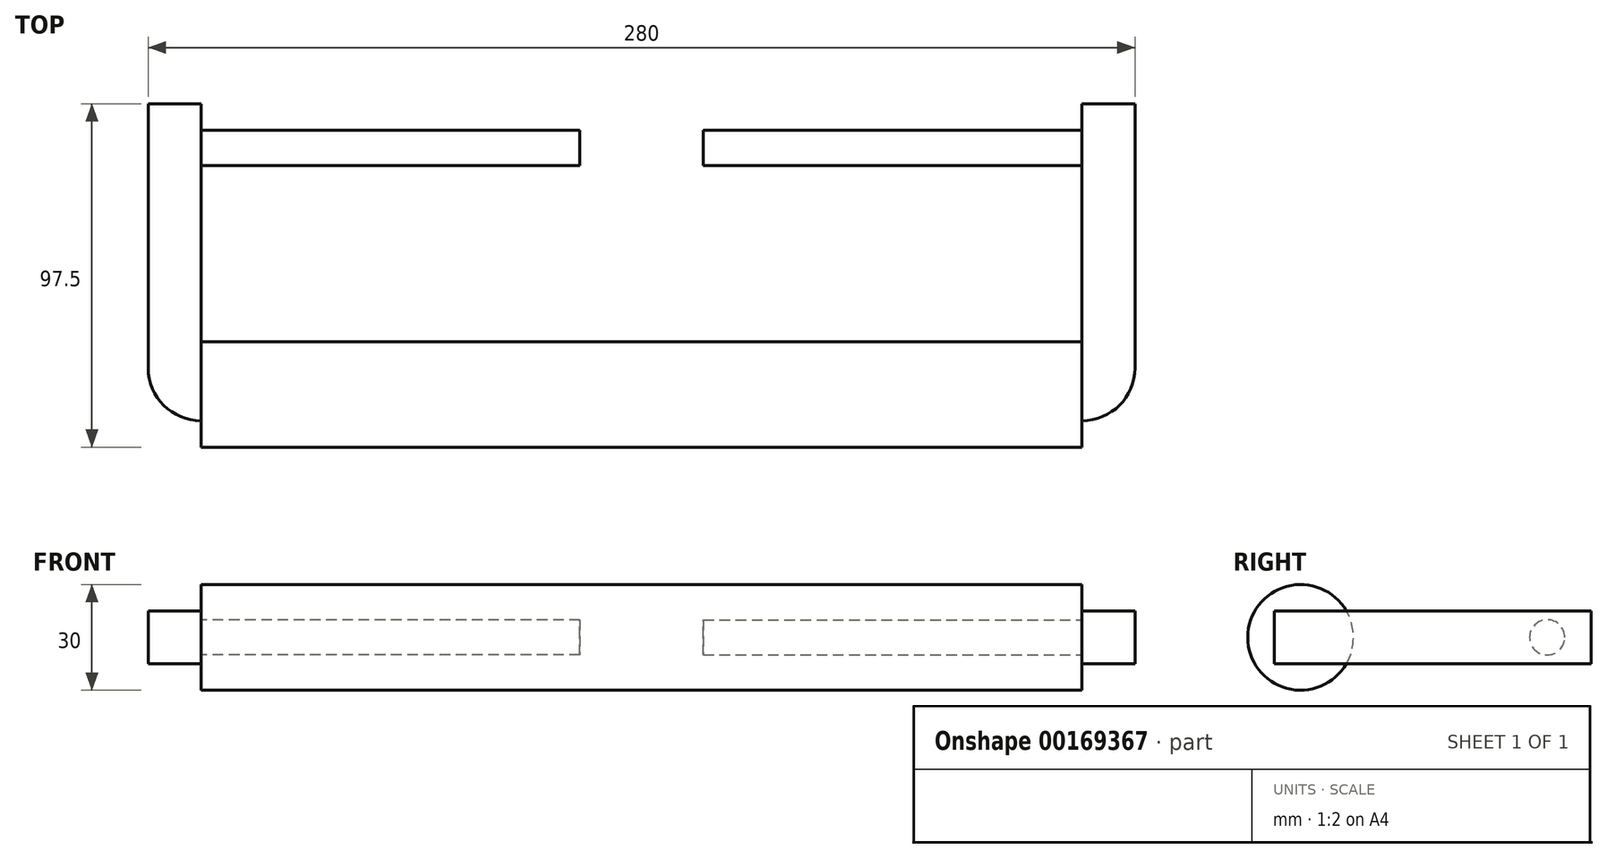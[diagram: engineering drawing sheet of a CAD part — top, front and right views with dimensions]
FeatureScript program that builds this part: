
annotation { "Feature Type Name" : "Feature", "Feature Type Description" : "" }
export const myFeature = defineFeature(function(context is Context, id is Id, definition is map)
    precondition{}
    {
        {
            var Q0;
            Q0=qCreatedBy(makeId("Right.planeOp"),FACE);
            var sketch = newSketch(context, id + "F0", { "sketchPlane" : qUnion([Q0])});
            skCircle(sketch, "E0", {"center": v(0, 0) * mm, "radius": 15 * mm});
            skSolve(sketch);
        }
        {
            var Q0;
            Q0=makeQuery(id+"F0.imprint","IMPRINT",FACE,{"disambiguationData":[TD([[makeQuery(id+"F0.imprint","IMPRINT",EDGE,{"derivedFrom":sQuery(id+"F0.wireOp",EDGE,"E0")}),1.0]])]});
            extrude(context, id + "F1", {"entities" : qUnion([Q0]), "endBound" : BoundingType.SYMMETRIC, "depth" : 250 * mm});
        }
        {
            var Q0;
            Q0=makeQuery(id+"F1.opExtrude","CAP_FACE",FACE,{"disambiguationData":[OSD([sQuery(id+"F0.wireOp",EDGE,"E0")])],"isStart":false});
            var sketch = newSketch(context, id + "F2", { "sketchPlane" : qUnion([Q0])});
            skLineSegment(sketch, "E1.bottom", {"start": v(7.5, -7.5) * mm, "end": v(-7.5, -7.5) * mm});
            skLineSegment(sketch, "E1.top", {"start": v(7.5, 7.5) * mm, "end": v(-7.5, 7.5) * mm});
            skLineSegment(sketch, "E1.left", {"start": v(7.5, -7.5) * mm, "end": v(7.5, 7.5) * mm});
            skLineSegment(sketch, "E1.right", {"start": v(-7.5, -7.5) * mm, "end": v(-7.5, 7.5) * mm});
            skPoint(sketch, "E1.middle", {"position": v(0, 0) * mm});
            skSolve(sketch);
        }
        {
            var Q0;
            Q0=qSketchRegion(id+"F2",true);
            var Q1;
            Q1=sQuery(id+"F2.wireOp",EDGE,"E1.left");
            revolve(context, id + "F3", {"entities" : qUnion([Q0]), "axis" : qUnion([Q1]), "revolveType" : RevolveType.ONE_DIRECTION, "angle" : 90 * degree});
        }
        {
            var Q0;
            Q0=makeQuery(id+"F3.opRevolve","SWEPT_BODY",BODY,{"disambiguationData":[OSD([sQuery(id+"F2.wireOp",EDGE,"E1.bottom"),sQuery(id+"F2.wireOp",EDGE,"E1.top"),sQuery(id+"F2.wireOp",EDGE,"E1.left"),sQuery(id+"F2.wireOp",EDGE,"E1.right")])]});
            var Q1;
            Q1=qCreatedBy(makeId("Right.planeOp"),FACE);
            mirror(context, id + "F4", {"operationType" : NewBodyOperationType.ADD, "entities" : qUnion([Q0]), "mirrorPlane" : qUnion([Q1])});
        }
        {
            var Q0;
            Q0=makeQuery(id+"F3.opRevolve","CAP_FACE",FACE,{"disambiguationData":[OSD([sQuery(id+"F2.wireOp",EDGE,"E1.bottom"),sQuery(id+"F2.wireOp",EDGE,"E1.top"),sQuery(id+"F2.wireOp",EDGE,"E1.left"),sQuery(id+"F2.wireOp",EDGE,"E1.right")])],"isStart":false});
            var sketch = newSketch(context, id + "F5", { "sketchPlane" : qUnion([Q0])});
            skLineSegment(sketch, "E2.bottom", {"start": v(-140, 7.5) * mm, "end": v(-125, 7.5) * mm});
            skLineSegment(sketch, "E2.top", {"start": v(-140, -7.5) * mm, "end": v(-125, -7.5) * mm});
            skLineSegment(sketch, "E2.left", {"start": v(-140, 7.5) * mm, "end": v(-140, -7.5) * mm});
            skLineSegment(sketch, "E2.right", {"start": v(-125, 7.5) * mm, "end": v(-125, -7.5) * mm});
            skSolve(sketch);
        }
        {
            var Q0;
            Q0=qSketchRegion(id+"F5",true);
            extrude(context, id + "F6", {"entities" : qUnion([Q0]), "operationType" : NewBodyOperationType.ADD, "depth" : 75 * mm});
        }
        {
            var Q0;
            Q0=makeQuery(id+"F1.opExtrude","SWEPT_BODY",BODY,{"disambiguationData":[OSD([sQuery(id+"F0.wireOp",EDGE,"E0")])]});
            var Q1;
            Q1=qCreatedBy(makeId("Right.planeOp"),FACE);
            mirror(context, id + "F7", {"operationType" : NewBodyOperationType.ADD, "entities" : qUnion([Q0]), "mirrorPlane" : qUnion([Q1])});
        }
        {
            var Q0;
            Q0=makeQuery(id+"F7.opPattern","COPY",FACE,{"derivedFrom":makeQuery(id+"F6.opExtrude","SWEPT_FACE",FACE,{"disambiguationData":[OSD([sQuery(id+"F5.wireOp",EDGE,"E2.left")])]}),"instanceName":"1"});
            var sketch = newSketch(context, id + "F8", { "sketchPlane" : qUnion([Q0])});
            skCircle(sketch, "E3", {"center": v(-70, 0) * mm, "radius": 5 * mm});
            skSolve(sketch);
        }
        {
            var Q0;
            Q0=qSketchRegion(id+"F8",true);
            extrude(context, id + "F9", {"entities" : qUnion([Q0]), "operationType" : NewBodyOperationType.ADD, "oppositeDirection" : true, "depth" : 122.5 * mm});
        }
        {
            var Q0;
            Q0=makeQuery(id+"F6.opExtrude","SWEPT_FACE",FACE,{"disambiguationData":[OSD([sQuery(id+"F5.wireOp",EDGE,"E2.left")])]});
            var sketch = newSketch(context, id + "F10", { "sketchPlane" : qUnion([Q0])});
            skCircle(sketch, "E4", {"center": v(70, 0) * mm, "radius": 5 * mm});
            skSolve(sketch);
        }
        {
            var Q0;
            Q0=makeQuery(id+"F10.imprint","IMPRINT",FACE,{"disambiguationData":[TD([[makeQuery(id+"F10.imprint","IMPRINT",EDGE,{"derivedFrom":sQuery(id+"F10.wireOp",EDGE,"E4")}),1.0]])]});
            extrude(context, id + "F11", {"entities" : qUnion([Q0]), "operationType" : NewBodyOperationType.ADD, "oppositeDirection" : true, "depth" : 122.5 * mm});
        }
    });
